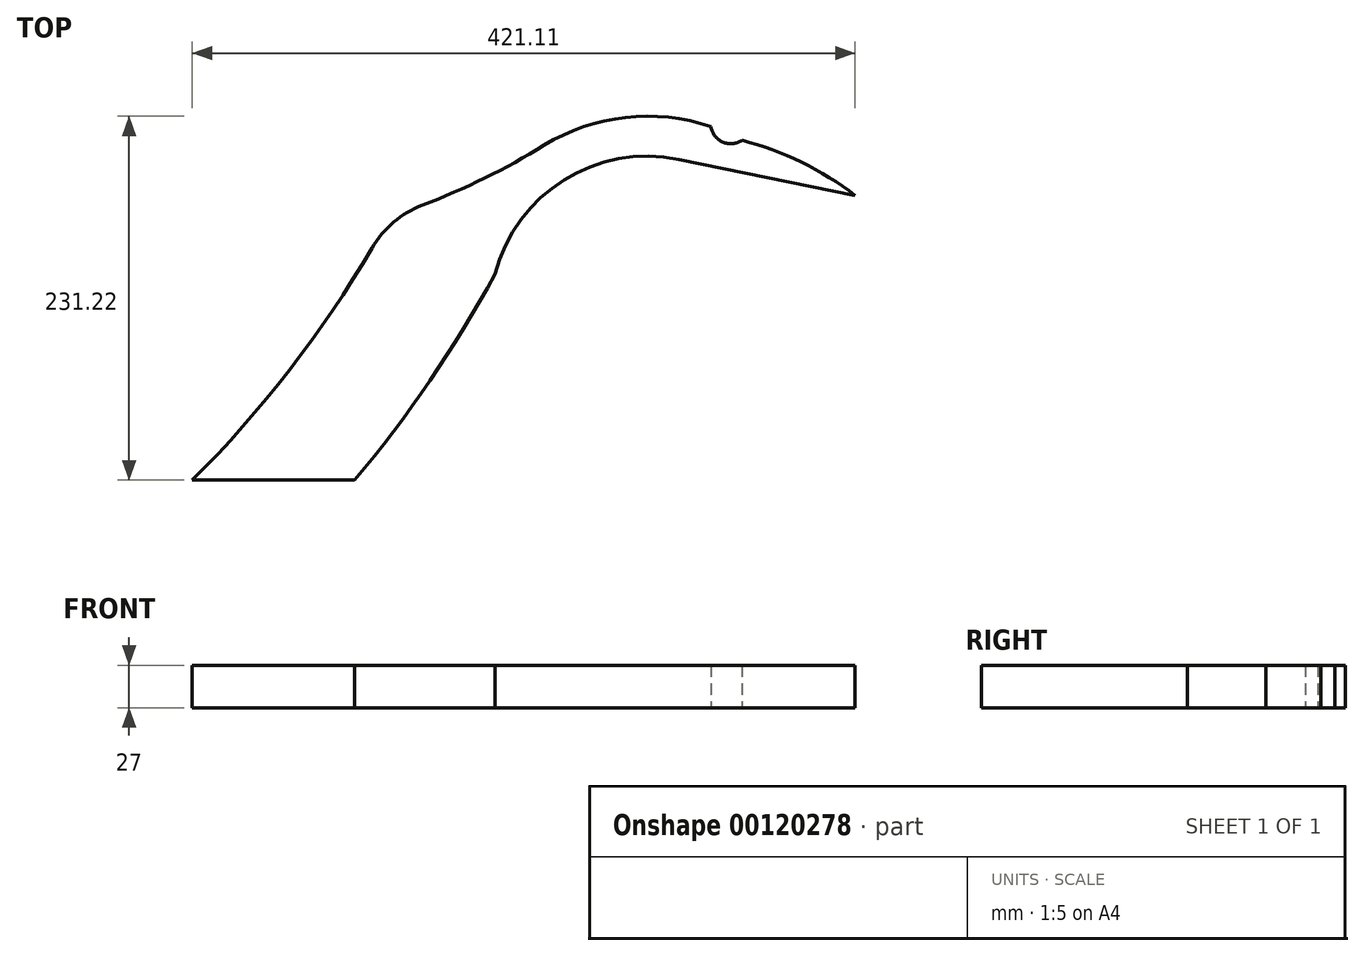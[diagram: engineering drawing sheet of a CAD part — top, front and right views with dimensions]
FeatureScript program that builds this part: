
annotation { "Feature Type Name" : "Feature", "Feature Type Description" : "" }
export const myFeature = defineFeature(function(context is Context, id is Id, definition is map)
    precondition{}
    {
        {
            var Q0;
            Q0=qCreatedBy(makeId("Top.planeOp"),FACE);
            var sketch = newSketch(context, id + "F0", { "sketchPlane" : qUnion([Q0])});
            skLineSegment(sketch, "E0.0.0", {"start": v(220, 203.8) * mm, "end": v(331.98, 180.9) * mm});
            skArc(sketch, "E0.0.1", {"start": v(331.98, 180.9) * mm, "mid": v(297.76, 202.02) * mm, "end": v(260.02, 215.9) * mm});
            skArc(sketch, "E0.0.2", {"start": v(260.02, 215.9) * mm, "mid": v(247.79, 214.8) * mm, "end": v(240.33, 224.55) * mm});
            skArc(sketch, "E0.0.3", {"start": v(240.33, 224.55) * mm, "mid": v(186.05, 230.45) * mm, "end": v(134.4, 212.72) * mm});
            skArc(sketch, "E0.0.4", {"start": v(134.4, 212.72) * mm, "mid": v(96.68, 191.93) * mm, "end": v(57.18, 174.71) * mm});
            skArc(sketch, "E0.0.5", {"start": v(25.04, 147.5) * mm, "mid": v(38.79, 163.84) * mm, "end": v(57.18, 174.71) * mm});
            skArc(sketch, "E0.0.6", {"start": v(25.04, 147.5) * mm, "mid": v(-75.16, 14.3) * mm, "end": v(-203.06, -92.57) * mm});
            skArc(sketch, "E0.0.7", {"start": v(-272.45, -246.2) * mm, "mid": v(-248.6, -164.48) * mm, "end": v(-203.06, -92.57) * mm});
            skLineSegment(sketch, "E0.0.8", {"start": v(-272.45, -246.2) * mm, "end": v(-253.42, -365.24) * mm});
            skArc(sketch, "E0.0.9", {"start": v(-253.42, -365.24) * mm, "mid": v(-248.03, -364.04) * mm, "end": v(-243.66, -360.66) * mm});
            skArc(sketch, "E0.0.10", {"start": v(-229.15, -283.97) * mm, "mid": v(-226.47, -324.2) * mm, "end": v(-243.66, -360.66) * mm});
            skArc(sketch, "E0.0.11", {"start": v(-229.15, -283.97) * mm, "mid": v(-222.5, -205.59) * mm, "end": v(-161.23, -156.26) * mm});
            skArc(sketch, "E0.0.12", {"start": v(103.14, 130.83) * mm, "mid": v(-11.34, -29.02) * mm, "end": v(-161.23, -156.26) * mm});
            skArc(sketch, "E0.0.13", {"start": v(103.14, 130.83) * mm, "mid": v(147, 190.65) * mm, "end": v(220, 203.8) * mm});
            skSolve(sketch);
        }
        {
            var Q0;
            Q0=makeQuery(id+"F0.imprint","IMPRINT",FACE,{"disambiguationData":[TD([[makeQuery(id+"F0.imprint","IMPRINT",EDGE,{"derivedFrom":sQuery(id+"F0.wireOp",EDGE,"E0.0.0")}),1.0]])]});
            extrude(context, id + "F1", {"entities" : qUnion([Q0]), "depth" : 27 * mm});
        }
        {
            var Q0;
            Q0=qCreatedBy(makeId("Top.planeOp"),FACE);
            var sketch = newSketch(context, id + "F2", { "sketchPlane" : qUnion([Q0])});
            skLineSegment(sketch, "E1.bottom", {"start": v(79.64, 0) * mm, "end": v(-323.44, 0) * mm});
            skLineSegment(sketch, "E1.top", {"start": v(79.64, -389.7) * mm, "end": v(-323.44, -389.7) * mm});
            skLineSegment(sketch, "E1.left", {"start": v(79.64, 0) * mm, "end": v(79.64, -389.7) * mm});
            skLineSegment(sketch, "E1.right", {"start": v(-323.44, 0) * mm, "end": v(-323.44, -389.7) * mm});
            skSolve(sketch);
        }
        {
            var Q0;
            Q0 = qSketchRegion(id + "F2", true);
            extrude(context, id + "F3", {"entities" : qUnion([Q0]), "operationType" : NewBodyOperationType.REMOVE, "depth" : 50 * mm});
        }
    });
